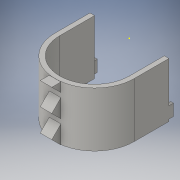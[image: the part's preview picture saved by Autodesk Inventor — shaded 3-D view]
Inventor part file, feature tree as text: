
AUTODESK INVENTOR PART (.ipt)
format: ipt  version: 2016 (Build 200138000, 138)  size: 223,232 bytes
history: native  units: in
note: dims shown in document units (in); Inventor stores cm internally (conversion verified against a paired STEP export)
features: sketch x10, reference x10, extrude x9, plane x1
ambient origin geometry x8: Origin, YZ Plane, XZ Plane, XY Plane, X Axis, Y Axis, Z Axis, Center Point
bodies: Solid1 (feature_tree)
feature tree (30):
  extrude  "Extrusion1"  Depth=1.5in TaperAngle=0.0deg
  extrude  "Extrusion2"  Depth=0.1969in TaperAngle=0.0deg
  extrude  "Extrusion3"  [1 undecoded]
  extrude  "Extrusion4"  Depth=0.3937in
  plane  "Work Plane1"
  sketch  "Sketch5"  dims[d12=1.9685in d14=0.9774in d15=0.3937in d17=1.0in d19=0.5in d20=0.0in]
  extrude  "Extrusion5"  Depth=0.5in TaperAngle=0.0deg
  extrude  "Extrusion6"  Depth=0.197in TaperAngle=0.0deg
  extrude  "Extrusion7"  Depth=16.0in TaperAngle=0.0deg
  extrude  "Extrusion8"  [1 undecoded]
  extrude  "Extrusion9"  [1 undecoded]
  sketch  "Sketch1"  dims[d0=0.1969in d1=1.5in d2=0.0in]
  reference  "Reference1"
  sketch  "Sketch2"  dims[d3=4.6969in d4=0.0in d5=0.1969in d6=0.0in]
  sketch  "Sketch3"  dims[d7=0.1969in d8=0.0in d9=-1.697in]
  sketch  "Sketch4"  dims[d10=0.7874in d11=0.3937in]
  reference  "Reference2"
  sketch  "Sketch6"  dims[d21=0.197in d22=0.0in d23=2.0in d24=0.0in]
  sketch  "Sketch8"  dims[d25=2.0in d26=0.0in d27=16.0in d28=0.0in]
  reference  "Reference3"
  reference  "Reference5"
  reference  "Reference6"
  reference  "Reference7"
  reference  "Reference8"
  reference  "Reference9"
  sketch  "Sketch9"
  reference  "Reference10"
  sketch  "Sketch10"
  reference  "Reference11"
  sketch  "Sketch11"
note: 3 required parameter values undecoded (feature->parameter linkage not recoverable at this tier; creation-order binding heuristic only, values carry confidence <= 0.55)
